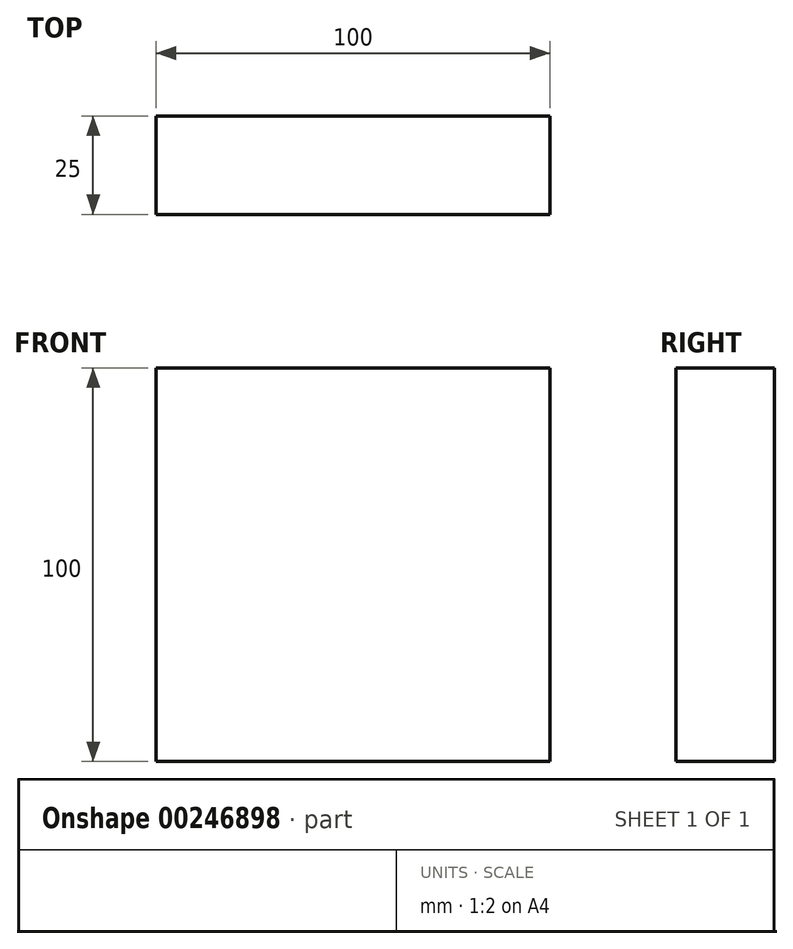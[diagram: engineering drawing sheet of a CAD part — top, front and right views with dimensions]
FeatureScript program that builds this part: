
annotation { "Feature Type Name" : "Feature", "Feature Type Description" : "" }
export const myFeature = defineFeature(function(context is Context, id is Id, definition is map)
    precondition{}
    {
        {
            var Q0;
            Q0=qCreatedBy(makeId("Front.planeOp"),FACE);
            var sketch = newSketch(context, id + "F0", { "sketchPlane" : qUnion([Q0])});
            skLineSegment(sketch, "E0.bottom", {"start": v(0, 0) * mm, "end": v(100, 0) * mm});
            skLineSegment(sketch, "E0.top", {"start": v(0, -100) * mm, "end": v(100, -100) * mm});
            skLineSegment(sketch, "E0.left", {"start": v(0, 0) * mm, "end": v(0, -100) * mm});
            skLineSegment(sketch, "E0.right", {"start": v(100, 0) * mm, "end": v(100, -100) * mm});
            skSolve(sketch);
        }
        {
            var Q0;
            Q0 = qSketchRegion(id + "F0", true);
            extrude(context, id + "F1", {"entities" : qUnion([Q0]), "depth" : 25 * mm});
        }
        {
            var Q0;
            Q0=makeQuery(id+"F1.opExtrude","CAP_FACE",FACE,{"disambiguationData":[OSD([sQuery(id+"F0.wireOp",EDGE,"E0.bottom"),sQuery(id+"F0.wireOp",EDGE,"E0.top"),sQuery(id+"F0.wireOp",EDGE,"E0.left"),sQuery(id+"F0.wireOp",EDGE,"E0.right")])],"isStart":false});
            var sketch = newSketch(context, id + "F2", { "sketchPlane" : qUnion([Q0])});
            skLineSegment(sketch, "E1", {"start": v(0, -53.35) * mm, "end": v(100, -53.35) * mm});
            skLineSegment(sketch, "E2", {"start": v(100, -53.35) * mm, "end": v(100, -43.35) * mm});
            skLineSegment(sketch, "E3", {"start": v(100, -43.35) * mm, "end": v(0, -43.35) * mm});
            skLineSegment(sketch, "E4", {"start": v(0, -43.35) * mm, "end": v(0, -53.35) * mm});
            skSolve(sketch);
        }
        {
            var Q0;
            Q0=makeQuery(id+"F2.imprint","IMPRINT",FACE,{"disambiguationData":[TD([[makeQuery(id+"F2.imprint","IMPRINT",EDGE,{"derivedFrom":sQuery(id+"F2.wireOp",EDGE,"E1")}),1.0]])]});
            var sketch = newSketch(context, id + "F3", { "sketchPlane" : qUnion([Q0])});
            skLineSegment(sketch, "E5", {"start": v(100.4, -43.2) * mm, "end": v(37.96, 47.78) * mm});
            skArc(sketch, "E6", {"start": v(37.96, 47.78) * mm, "mid": v(2, 8.93) * mm, "end": v(0, -43.97) * mm});
            skSolve(sketch);
        }
        {
            var Q0;
            Q0=sQuery(id+"F3.wireOp",EDGE,"E5");
            var Q1;
            Q1=sQuery(id+"F3.wireOp",EDGE,"E6");
            extrude(context, id + "F4", {"bodyType" : ToolBodyType.SURFACE, "operationType" : NewBodyOperationType.REMOVE, "surfaceEntities" : qUnion([Q0, Q1]), "oppositeDirection" : true, "depth" : 50 * mm});
        }
    });
